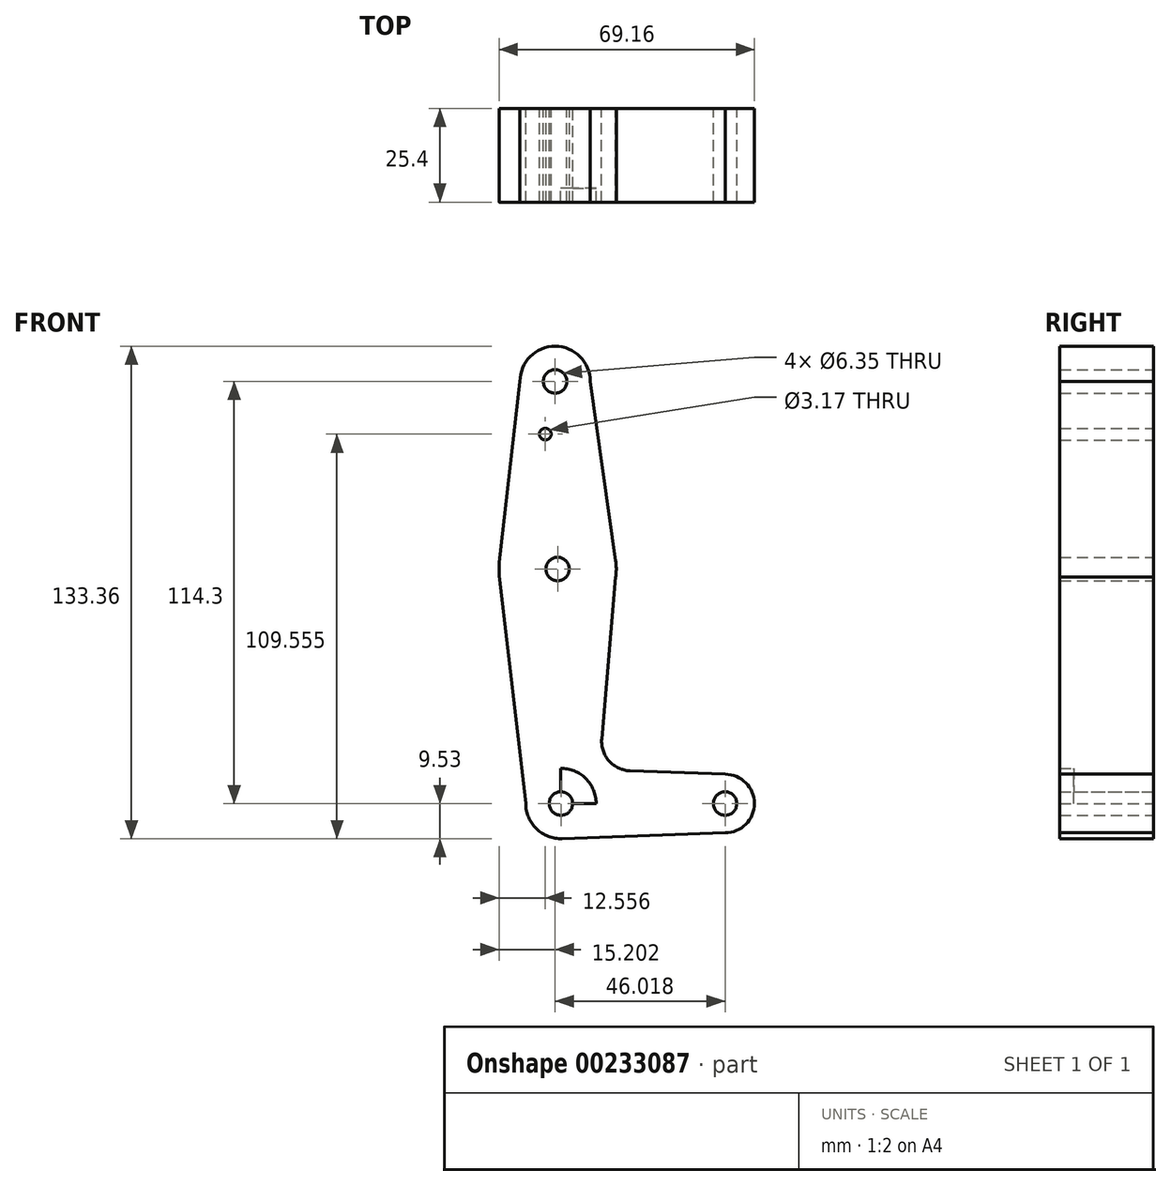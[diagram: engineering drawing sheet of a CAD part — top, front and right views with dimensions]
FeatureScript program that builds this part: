
annotation { "Feature Type Name" : "Feature", "Feature Type Description" : "" }
export const myFeature = defineFeature(function(context is Context, id is Id, definition is map)
    precondition{}
    {
        {
            var Q0;
            Q0=qCreatedBy(makeId("Front.planeOp"),FACE);
            var sketch = newSketch(context, id + "F0", { "sketchPlane" : qUnion([Q0])});
            skCircle(sketch, "E0", {"center": v(-46.02, 114.3) * mm, "radius": 9.53 * mm});
            skCircle(sketch, "E1", {"center": v(-46.02, 114.3) * mm, "radius": 3.18 * mm});
            skCircle(sketch, "E2", {"center": v(-45.35, 63.5) * mm, "radius": 3.18 * mm});
            skCircle(sketch, "E3", {"center": v(-44.45, 0) * mm, "radius": 3.18 * mm});
            skCircle(sketch, "E4", {"center": v(-48.66, 100.03) * mm, "radius": 1.59 * mm});
            skCircle(sketch, "E5", {"center": v(0, 0) * mm, "radius": 3.18 * mm});
            skCircle(sketch, "E6", {"center": v(-44.45, 0) * mm, "radius": 9.53 * mm});
            skCircle(sketch, "E7", {"center": v(-45.35, 63.5) * mm, "radius": 15.88 * mm});
            skLineSegment(sketch, "E8", {"start": v(-55.54, 114.3) * mm, "end": v(-61.12, 65.3) * mm});
            skLineSegment(sketch, "E9", {"start": v(-36.5, 114.3) * mm, "end": v(-29.63, 65.72) * mm});
            skLineSegment(sketch, "E10", {"start": v(-46.02, 114.3) * mm, "end": v(-45.35, 63.5) * mm});
            skCircle(sketch, "E11", {"center": v(0, 0) * mm, "radius": 7.94 * mm});
            skLineSegment(sketch, "E12", {"start": v(-29.63, 61.28) * mm, "end": v(-33.39, 17.49) * mm});
            skLineSegment(sketch, "E13", {"start": v(-45.35, 63.5) * mm, "end": v(-44.45, 0) * mm});
            skLineSegment(sketch, "E14", {"start": v(-44.45, 0) * mm, "end": v(0, 0) * mm});
            skLineSegment(sketch, "E15", {"start": v(-53.98, 0) * mm, "end": v(-61.12, 61.67) * mm});
            skLineSegment(sketch, "E16", {"start": v(0, 7.94) * mm, "end": v(-25.75, 8.86) * mm});
            skLineSegment(sketch, "E17", {"start": v(0, -7.94) * mm, "end": v(-44.1, -9.52) * mm});
            skPoint(sketch, "E18.newPointA", {"position": v(-34.89, 0) * mm});
            skArc(sketch, "E18.filletArc", {"start": v(-33.39, 17.49) * mm, "mid": v(-31.42, 11.54) * mm, "end": v(-25.75, 8.86) * mm});
            skSolve(sketch);
        }
        {
            var Q0;
            Q0 = qSketchRegion(id + "F0", true);
            extrude(context, id + "F1", {"entities" : qUnion([Q0]), "depth" : 25.4 * mm});
        }
        {
            var Q0;
            Q0 = qSketchRegion(id + "F0", true);
            var Q1;
            {var subQ0=sQuery(id+"F0.wireOp",EDGE,"E13");var subQ1=sQuery(id+"F0.wireOp",EDGE,"E3");var subQ2=makeQuery(id+"F0.imprint","INTERSECT",VERTEX,{"derivedFrom":[subQ1,subQ0]});Q1=makeQuery(id+"F0.imprint","IMPRINT",FACE,{"disambiguationData":[TD([[makeQuery(id+"F0.imprint","IMPRINT",EDGE,{"disambiguationData":[TD([[subQ2,1.0]])],"derivedFrom":subQ1}),-1.0]])]});}
            extrude(context, id + "F2", {"entities" : qUnion([Q0, Q1]), "operationType" : NewBodyOperationType.ADD, "depth" : 21.59 * mm});
        }
    });
